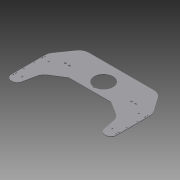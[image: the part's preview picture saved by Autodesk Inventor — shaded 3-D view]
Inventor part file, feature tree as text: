
AUTODESK INVENTOR PART (.ipt)
format: ipt  version: 2015 (Build 190159000, 159)  size: 313,856 bytes
history: native  units: mm
features: extrude x1, sketch x1
ambient origin geometry x8: Origin, YZ Plane, XZ Plane, XY Plane, X Axis, Y Axis, Z Axis, Center Point
bodies: Body1 (feature_tree)
feature tree (2):
  extrude  "Extrusion25"  Depth=3.0mm TaperAngle=0.0deg
  sketch  "Sketch44"  dims[d19=5.0mm d127=97.0mm d151=5.0mm d163=5.0mm d222=5.0mm d248=40.0mm d294=25.0mm d324=5.0mm d326=25.0mm d329=25.0mm d344=6.0mm d358=6.0mm d404=5.0mm d406=45.0mm d445=20.0mm d446=30.0mm d448=45.0deg d460=5.606189mm d463=30.0deg d467=42.0mm d468=36.0mm d469=150.0deg d483=12.0mm d486=42.0mm d487=150.0deg d488=36.0mm d489=150.0deg d528=20.0mm d530=65.0mm d726=80.0mm d727=50.0mm d728=200.0mm d729=100.0mm d730=70.0mm d731=180.0mm d732=20.0mm d733=100.0mm d734=50.0mm d735=50.0mm d736=25.0mm d737=5.0mm d738=5.0mm d739=150.0mm d740=5.0mm d741=5.0mm d742=30.0mm d743=10.0mm d744=6.0mm d745=97.0mm d746=73.0mm d747=4.0mm d748=8.0mm d749=8.0mm d750=7.0mm d751=4.0mm d752=8.0mm d753=8.0mm d754=1.0mm d755=8.0mm d756=4.0mm d757=7.0mm d758=8.0mm d759=4.0mm d760=8.0mm d761=30.0mm d762=8.0mm d763=1.0mm d764=30.0mm d765=8.0mm d766=4.0mm d767=8.0mm d768=4.0mm d769=30.0mm d770=7.0mm d771=5.0mm d772=8.0mm d773=4.0mm d774=8.0mm d775=4.0mm d776=30.0mm d777=7.0mm d778=5.0mm d779=90.0mm d780=97.0mm d781=6.0mm d782=10.0mm d783=73.0mm d784=65.0mm d785=100.0mm d786=200.0mm d787=5.0mm d788=2.5mm d789=50.0mm d790=2.5mm d791=5.0mm d792=5.0mm d793=50.0mm d794=5.0mm d795=5.0mm d796=50.0mm d797=5.0mm d798=5.0mm d799=50.0mm d800=5.0mm d801=5.0mm d802=50.0mm d803=10.0mm d804=6.0mm d805=10.0mm d806=10.0mm d807=10.0mm d808=6.0mm d809=3.0mm d810=0.0mm]
